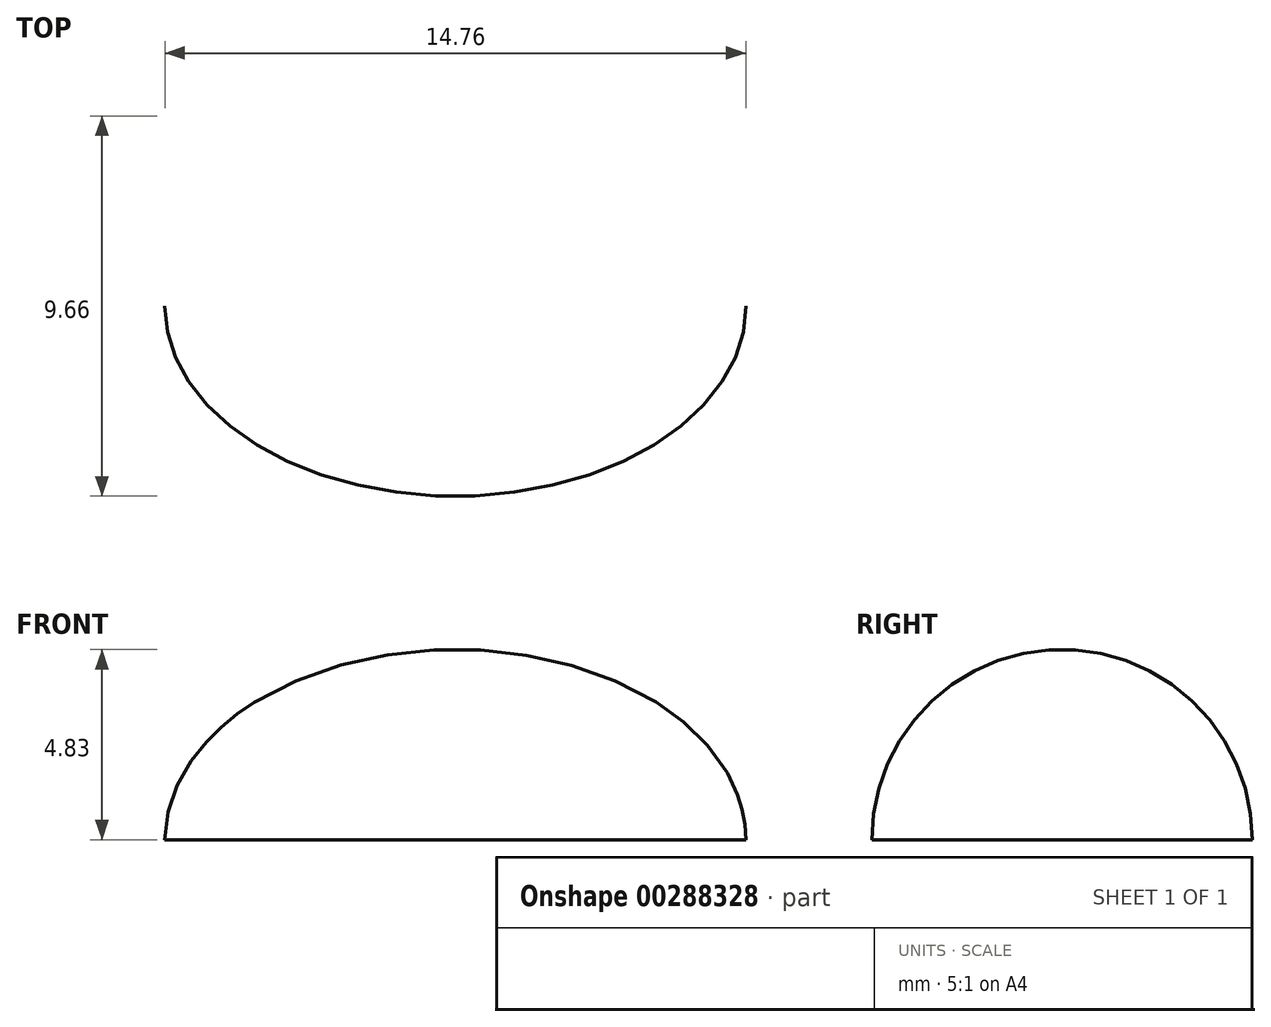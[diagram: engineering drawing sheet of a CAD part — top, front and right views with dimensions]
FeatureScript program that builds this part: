
annotation { "Feature Type Name" : "Feature", "Feature Type Description" : "" }
export const myFeature = defineFeature(function(context is Context, id is Id, definition is map)
    precondition{}
    {
        {
            var Q0;
            Q0=qCreatedBy(makeId("Top.planeOp"),FACE);
            var sketch = newSketch(context, id + "F0", { "sketchPlane" : qUnion([Q0])});
            skEllipticalArc(sketch, "E0", {});
            skLineSegment(sketch, "E1", {"start": v(-7.38, 0) * mm, "end": v(7.38, 0) * mm});
            const initialGuessF0  = {"E0": [0, 0, -1, 0, 0.007383472286164761, 0.0048336176347790125, 0, 3.141592653589793]};
            skSetInitialGuess(sketch, initialGuessF0);
            skSolve(sketch);
        }
        {
            var Q0;
            Q0=makeQuery(id+"F0.imprint","IMPRINT",FACE,{"disambiguationData":[TD([[makeQuery(id+"F0.imprint","IMPRINT",EDGE,{"derivedFrom":sQuery(id+"F0.wireOp",EDGE,"E0")}),1.0]])]});
            var Q1;
            Q1=sQuery(id+"F0.wireOp",EDGE,"E1");
            revolve(context, id + "F1", {"entities" : qUnion([Q0]), "axis" : qUnion([Q1]), "revolveType" : RevolveType.ONE_DIRECTION, "oppositeDirection" : true, "angle" : 180 * degree});
        }
    });
